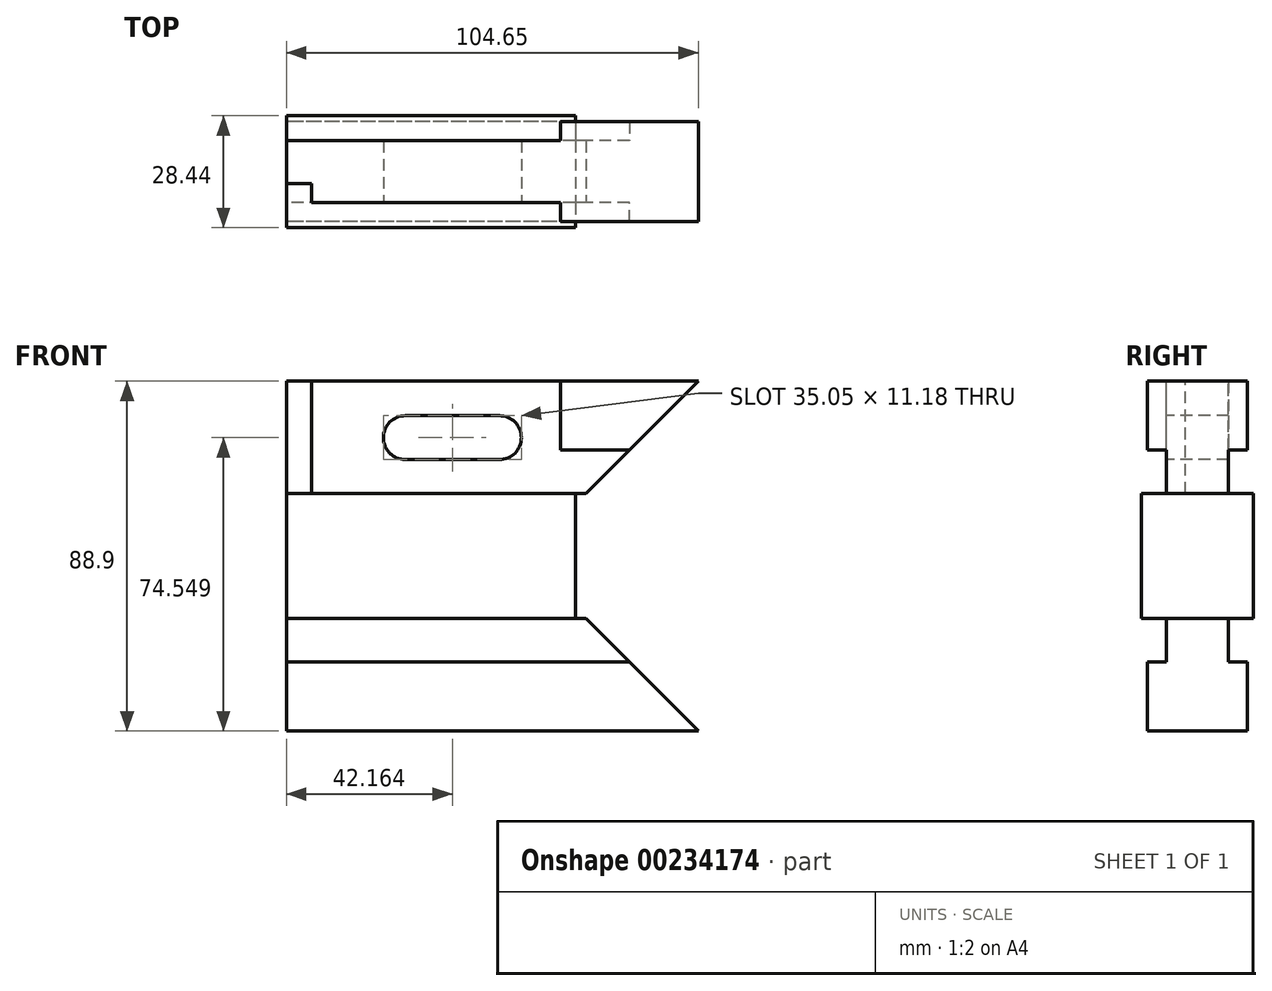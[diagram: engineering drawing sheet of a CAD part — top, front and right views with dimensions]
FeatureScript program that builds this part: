
annotation { "Feature Type Name" : "Feature", "Feature Type Description" : "" }
export const myFeature = defineFeature(function(context is Context, id is Id, definition is map)
    precondition{}
    {
        {
            var Q0;
            Q0=qCreatedBy(makeId("Right.planeOp"),FACE);
            var sketch = newSketch(context, id + "F0", { "sketchPlane" : qUnion([Q0])});
            skLineSegment(sketch, "E0", {"start": v(0, 44.45) * mm, "end": v(0, -47.4) * mm, "construction": true});
            skLineSegment(sketch, "E1", {"start": v(0, 44.45) * mm, "end": v(12.7, 44.45) * mm});
            skLineSegment(sketch, "E2", {"start": v(12.7, 44.45) * mm, "end": v(12.7, 26.92) * mm});
            skLineSegment(sketch, "E3", {"start": v(12.7, 26.92) * mm, "end": v(7.87, 26.92) * mm});
            skLineSegment(sketch, "E4", {"start": v(7.87, 26.92) * mm, "end": v(7.87, 15.88) * mm});
            skLineSegment(sketch, "E5", {"start": v(7.87, 15.88) * mm, "end": v(14.22, 15.88) * mm});
            skLineSegment(sketch, "E6", {"start": v(14.22, 15.88) * mm, "end": v(14.22, 0) * mm});
            skLineSegment(sketch, "E7", {"start": v(0, 0) * mm, "end": v(26.63, 0) * mm, "construction": true});
            skLineSegment(sketch, "E8.MirrorCS", {"start": v(0, -44.45) * mm, "end": v(12.7, -44.45) * mm});
            skLineSegment(sketch, "E9.MirrorCS", {"start": v(12.7, -44.45) * mm, "end": v(12.7, -26.92) * mm});
            skLineSegment(sketch, "E10.MirrorCS", {"start": v(12.7, -26.92) * mm, "end": v(7.87, -26.92) * mm});
            skLineSegment(sketch, "E11.MirrorCS", {"start": v(7.87, -26.92) * mm, "end": v(7.87, -15.88) * mm});
            skLineSegment(sketch, "E12.MirrorCS", {"start": v(7.87, -15.88) * mm, "end": v(14.22, -15.88) * mm});
            skLineSegment(sketch, "E13.MirrorCS", {"start": v(14.22, -15.88) * mm, "end": v(14.22, 0) * mm});
            skLineSegment(sketch, "E14.MirrorCS", {"start": v(-12.7, -26.92) * mm, "end": v(-7.87, -26.92) * mm});
            skLineSegment(sketch, "E15.MirrorCS", {"start": v(-12.7, 26.92) * mm, "end": v(-7.87, 26.92) * mm});
            skLineSegment(sketch, "E16.MirrorCS", {"start": v(0, 44.45) * mm, "end": v(-12.7, 44.45) * mm});
            skLineSegment(sketch, "E17.MirrorCS", {"start": v(-14.22, -15.88) * mm, "end": v(-14.22, 0) * mm});
            skLineSegment(sketch, "E18.MirrorCS", {"start": v(-12.7, 44.45) * mm, "end": v(-12.7, 26.92) * mm});
            skLineSegment(sketch, "E19.MirrorCS", {"start": v(-7.87, -26.92) * mm, "end": v(-7.87, -15.88) * mm});
            skLineSegment(sketch, "E20.MirrorCS", {"start": v(-7.87, -15.88) * mm, "end": v(-14.22, -15.88) * mm});
            skLineSegment(sketch, "E21.MirrorCS", {"start": v(-12.7, -44.45) * mm, "end": v(-12.7, -26.92) * mm});
            skLineSegment(sketch, "E22.MirrorCS", {"start": v(-14.22, 15.88) * mm, "end": v(-14.22, 0) * mm});
            skLineSegment(sketch, "E23.MirrorCS", {"start": v(-7.87, 15.88) * mm, "end": v(-14.22, 15.88) * mm});
            skLineSegment(sketch, "E24.MirrorCS", {"start": v(0, -44.45) * mm, "end": v(-12.7, -44.45) * mm});
            skLineSegment(sketch, "E25.MirrorCS", {"start": v(-7.87, 26.92) * mm, "end": v(-7.87, 15.88) * mm});
            skSolve(sketch);
        }
        {
            var Q0;
            Q0=qSketchRegion(id+"F0",true);
            extrude(context, id + "F1", {"entities" : qUnion([Q0]), "depth" : 104.65 * mm});
        }
        {
            var Q0;
            Q0=makeQuery(id+"F1.opExtrude","SWEPT_FACE",FACE,{"disambiguationData":[OSD([sQuery(id+"F0.wireOp",EDGE,"E17.MirrorCS"),sQuery(id+"F0.wireOp",EDGE,"E22.MirrorCS")])]});
            var sketch = newSketch(context, id + "F2", { "sketchPlane" : qUnion([Q0])});
            skLineSegment(sketch, "E26", {"start": v(0, 0) * mm, "end": v(146.66, 0) * mm, "construction": true});
            skLineSegment(sketch, "E27", {"start": v(73.4, 0) * mm, "end": v(73.4, 15.87) * mm});
            skLineSegment(sketch, "E28", {"start": v(73.4, 15.87) * mm, "end": v(76.07, 15.87) * mm});
            skLineSegment(sketch, "E29", {"start": v(104.65, 15.87) * mm, "end": v(104.65, 0) * mm});
            skLineSegment(sketch, "E30", {"start": v(104.65, 15.87) * mm, "end": v(104.65, 44.45) * mm});
            skLineSegment(sketch, "E31", {"start": v(76.07, 15.87) * mm, "end": v(104.65, 44.45) * mm});
            skLineSegment(sketch, "E32.MirrorCS", {"start": v(73.4, -15.87) * mm, "end": v(76.07, -15.87) * mm});
            skLineSegment(sketch, "E33.MirrorCS", {"start": v(104.65, -15.87) * mm, "end": v(104.65, -44.45) * mm});
            skLineSegment(sketch, "E34.MirrorCS", {"start": v(76.07, -15.87) * mm, "end": v(104.65, -44.45) * mm});
            skLineSegment(sketch, "E35.MirrorCS", {"start": v(73.4, 0) * mm, "end": v(73.4, -15.87) * mm});
            skLineSegment(sketch, "E36.MirrorCS", {"start": v(104.65, -15.87) * mm, "end": v(104.65, 0) * mm});
            skSolve(sketch);
        }
        {
            var Q0;
            Q0=qSketchRegion(id+"F2",true);
            extrude(context, id + "F3", {"entities" : qUnion([Q0]), "operationType" : NewBodyOperationType.REMOVE, "endBound" : BoundingType.THROUGH_ALL, "oppositeDirection" : true, "depth" : 25.4 * mm});
        }
        {
            var Q0;
            Q0=makeQuery(id+"F1.opExtrude","SWEPT_FACE",FACE,{"disambiguationData":[OSD([sQuery(id+"F0.wireOp",EDGE,"E1"),sQuery(id+"F0.wireOp",EDGE,"E16.MirrorCS")])]});
            cPlane(context, id + "F4", {"entities" : qUnion([Q0]), "cplaneType" : CPlaneType.OFFSET, "offset" : 44.45 * mm, "oppositeDirection" : true, "width" : 152.4 * mm, "height" : 152.4 * mm});
        }
        {
            var Q0;
            Q0=makeQuery(id+"F1.opExtrude","SWEPT_FACE",FACE,{"disambiguationData":[OSD([sQuery(id+"F0.wireOp",EDGE,"E1"),sQuery(id+"F0.wireOp",EDGE,"E16.MirrorCS")])]});
            var sketch = newSketch(context, id + "F5", { "sketchPlane" : qUnion([Q0])});
            skLineSegment(sketch, "E37.bottom", {"start": v(0, 12.7) * mm, "end": v(69.6, 12.7) * mm});
            skLineSegment(sketch, "E37.top", {"start": v(0, 7.87) * mm, "end": v(69.6, 7.87) * mm});
            skLineSegment(sketch, "E37.left", {"start": v(0, 12.7) * mm, "end": v(0, 7.87) * mm});
            skLineSegment(sketch, "E37.right", {"start": v(69.6, 12.7) * mm, "end": v(69.6, 7.87) * mm});
            skLineSegment(sketch, "E38", {"start": v(0, 0) * mm, "end": v(86.93, 0) * mm, "construction": true});
            skLineSegment(sketch, "E39.MirrorCS", {"start": v(0, -12.7) * mm, "end": v(69.6, -12.7) * mm});
            skLineSegment(sketch, "E40.MirrorCS", {"start": v(6.35, -7.87) * mm, "end": v(69.6, -7.87) * mm});
            skLineSegment(sketch, "E41.MirrorCS", {"start": v(69.6, -12.7) * mm, "end": v(69.6, -7.87) * mm});
            skLineSegment(sketch, "E42", {"start": v(0, -3.05) * mm, "end": v(6.35, -3.05) * mm});
            skLineSegment(sketch, "E43", {"start": v(6.35, -3.05) * mm, "end": v(6.35, -7.87) * mm});
            skLineSegment(sketch, "E44", {"start": v(0, -3.05) * mm, "end": v(0, -12.7) * mm});
            skSolve(sketch);
        }
        {
            var Q0;
            Q0=qSketchRegion(id+"F5",true);
            extrude(context, id + "F6", {"entities" : qUnion([Q0]), "operationType" : NewBodyOperationType.REMOVE, "oppositeDirection" : true, "depth" : 28.57 * mm});
        }
        {
            var Q0;
            Q0=makeQuery(id+"F6.boolean.opBoolean","MERGE",FACE,{"derivedFrom":[makeQuery(id+"F1.opExtrude","SWEPT_FACE",FACE,{"disambiguationData":[OSD([sQuery(id+"F0.wireOp",EDGE,"E25.MirrorCS")])]}),makeQuery(id+"F6.opExtrude","SWEPT_FACE",FACE,{"disambiguationData":[OSD([sQuery(id+"F5.wireOp",EDGE,"E40.MirrorCS")])]})]});
            var sketch = newSketch(context, id + "F7", { "sketchPlane" : qUnion([Q0])});
            skArc(sketch, "E45", {"start": v(30.23, 35.69) * mm, "mid": v(24.64, 30.1) * mm, "end": v(30.23, 24.51) * mm});
            skLineSegment(sketch, "E46", {"start": v(30.23, 30.1) * mm, "end": v(42.16, 30.1) * mm, "construction": true});
            skLineSegment(sketch, "E47", {"start": v(30.23, 35.69) * mm, "end": v(42.16, 35.69) * mm});
            skLineSegment(sketch, "E48.MirrorCS", {"start": v(30.23, 24.51) * mm, "end": v(42.16, 24.51) * mm});
            skLineSegment(sketch, "E49", {"start": v(42.16, 35.69) * mm, "end": v(42.16, 24.51) * mm, "construction": true});
            skLineSegment(sketch, "E50.MirrorCS", {"start": v(54.1, 30.1) * mm, "end": v(42.16, 30.1) * mm, "construction": true});
            skArc(sketch, "E51.MirrorCS", {"start": v(54.1, 35.69) * mm, "mid": v(59.7, 30.1) * mm, "end": v(54.1, 24.51) * mm});
            skLineSegment(sketch, "E52.MirrorCS", {"start": v(54.1, 35.69) * mm, "end": v(42.16, 35.69) * mm});
            skLineSegment(sketch, "E53.MirrorCS", {"start": v(54.1, 24.51) * mm, "end": v(42.16, 24.51) * mm});
            skSolve(sketch);
        }
        {
            var Q0;
            Q0=makeQuery(id+"F7.imprint","IMPRINT",FACE,{"disambiguationData":[TD([[makeQuery(id+"F7.imprint","IMPRINT",EDGE,{"derivedFrom":sQuery(id+"F7.wireOp",EDGE,"E45")}),1.0]])]});
            extrude(context, id + "F8", {"entities" : qUnion([Q0]), "operationType" : NewBodyOperationType.REMOVE, "endBound" : BoundingType.THROUGH_ALL, "oppositeDirection" : true, "depth" : 25.4 * mm});
        }
    });
